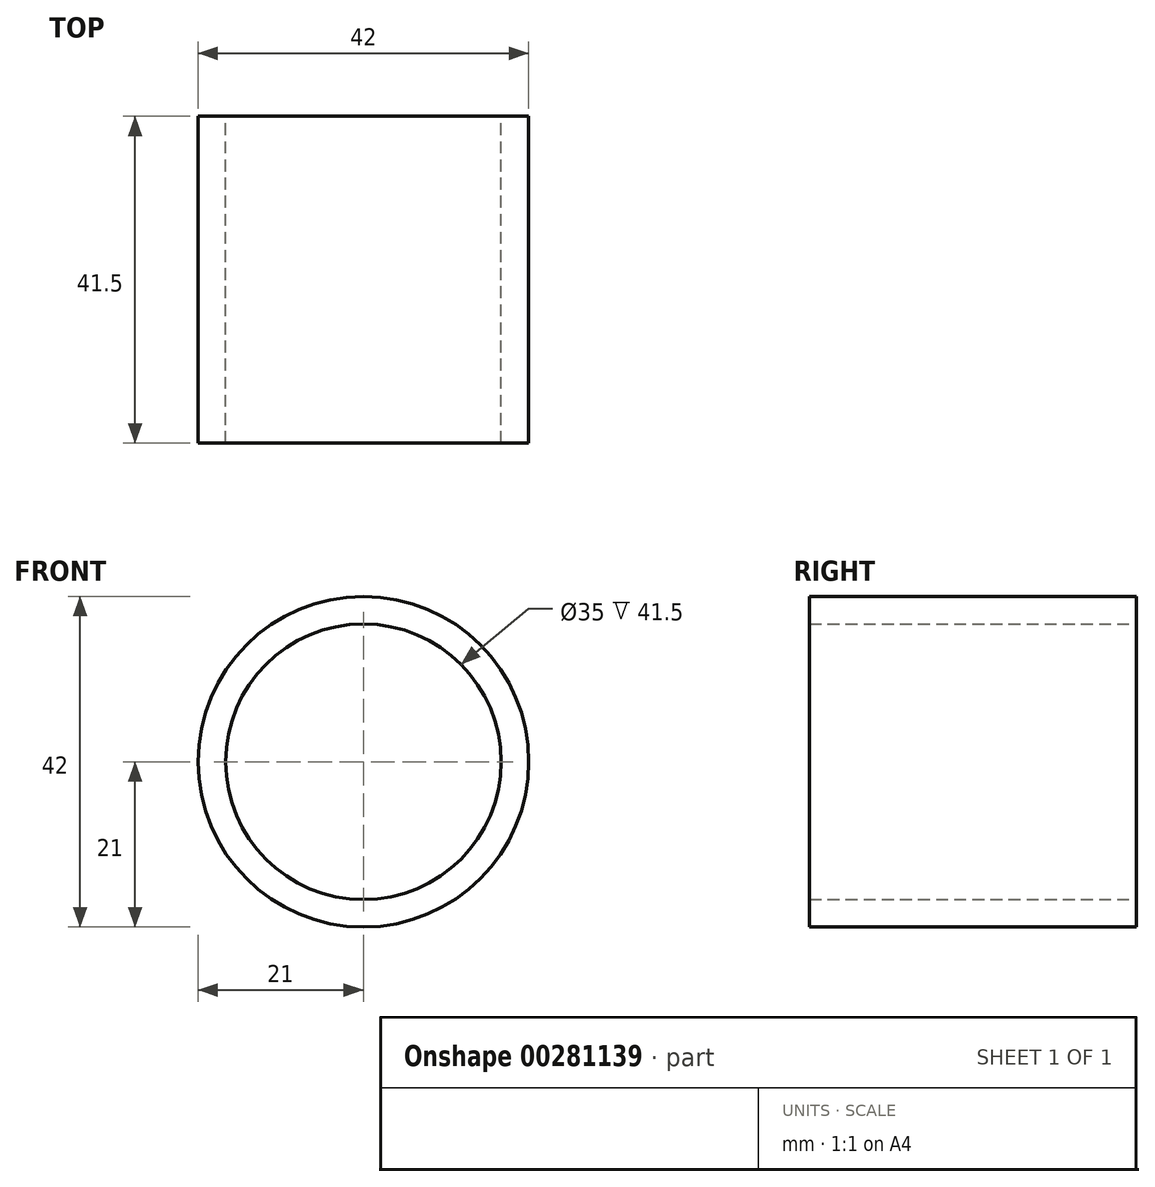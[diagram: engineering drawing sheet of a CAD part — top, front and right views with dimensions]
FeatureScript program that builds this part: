
annotation { "Feature Type Name" : "Feature", "Feature Type Description" : "" }
export const myFeature = defineFeature(function(context is Context, id is Id, definition is map)
    precondition{}
    {
        {
            var Q0;
            Q0=qCreatedBy(makeId("Front.planeOp"),FACE);
            var sketch = newSketch(context, id + "F0", { "sketchPlane" : qUnion([Q0])});
            skCircle(sketch, "E0", {"center": v(0, 0) * mm, "radius": 17.5 * mm});
            skCircle(sketch, "E1", {"center": v(0, 0) * mm, "radius": 21 * mm});
            skSolve(sketch);
        }
        {
            var Q0;
            Q0=makeQuery(id+"F0.imprint","IMPRINT",FACE,{"disambiguationData":[TD([[makeQuery(id+"F0.imprint","IMPRINT",EDGE,{"derivedFrom":sQuery(id+"F0.wireOp",EDGE,"E0")}),-1.0]])]});
            extrude(context, id + "F1", {"entities" : qUnion([Q0]), "depth" : 41.5 * mm});
        }
    });
